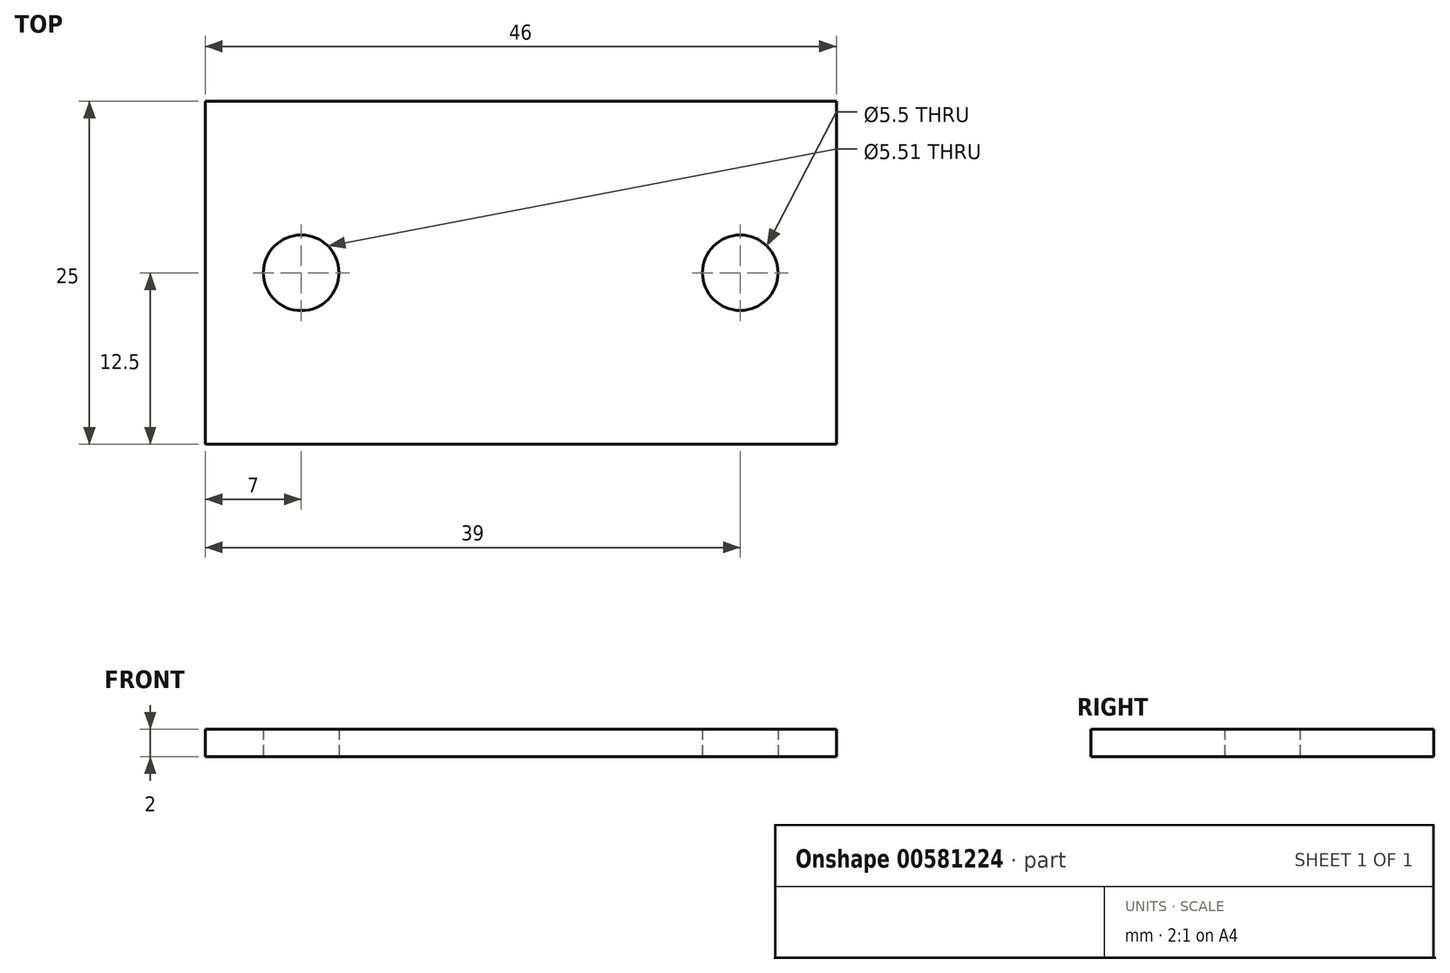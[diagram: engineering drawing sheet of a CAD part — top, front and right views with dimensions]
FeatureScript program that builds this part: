
annotation { "Feature Type Name" : "Feature", "Feature Type Description" : "" }
export const myFeature = defineFeature(function(context is Context, id is Id, definition is map)
    precondition{}
    {
        {
            var Q0;
            Q0=qCreatedBy(makeId("Top.planeOp"),FACE);
            var sketch = newSketch(context, id + "F0", { "sketchPlane" : qUnion([Q0])});
            skLineSegment(sketch, "E0.bottom", {"start": v(23, 12.5) * mm, "end": v(-23, 12.5) * mm});
            skLineSegment(sketch, "E0.top", {"start": v(23, -12.5) * mm, "end": v(-23, -12.5) * mm});
            skLineSegment(sketch, "E0.left", {"start": v(23, 12.5) * mm, "end": v(23, -12.5) * mm});
            skLineSegment(sketch, "E0.right", {"start": v(-23, 12.5) * mm, "end": v(-23, -12.5) * mm});
            skPoint(sketch, "E0.middle", {"position": v(0, 0) * mm});
            skCircle(sketch, "E1", {"center": v(16, 0) * mm, "radius": 2.75 * mm});
            skCircle(sketch, "E2.MirrorC", {"center": v(-16, 0) * mm, "radius": 2.76 * mm});
            skSolve(sketch);
        }
        {
            var Q0;
            Q0=qSketchRegion(id+"F0",true);
            extrude(context, id + "F1", {"entities" : qUnion([Q0]), "depth" : 2 * mm, "offsetDistance" : 25.4 * mm});
        }
    });
